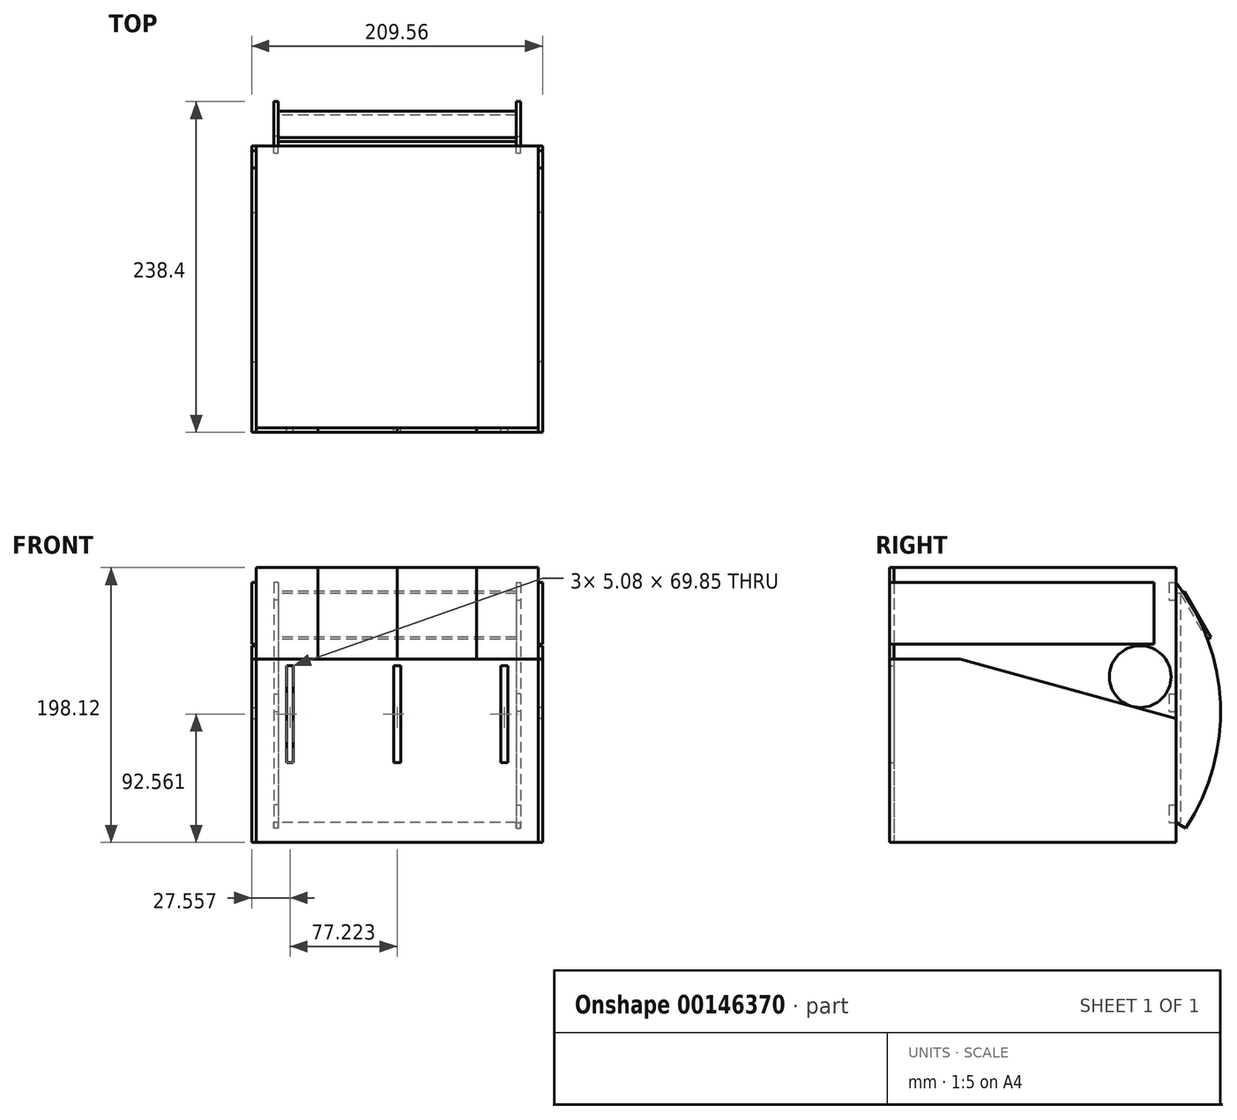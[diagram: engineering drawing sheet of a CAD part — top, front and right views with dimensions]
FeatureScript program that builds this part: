
annotation { "Feature Type Name" : "Feature", "Feature Type Description" : "" }
export const myFeature = defineFeature(function(context is Context, id is Id, definition is map)
    precondition{}
    {
        {
            var Q0;
            Q0=qCreatedBy(makeId("Top.planeOp"),FACE);
            var sketch = newSketch(context, id + "F0", { "sketchPlane" : qUnion([Q0])});
            skLineSegment(sketch, "E0.bottom", {"start": v(101.6, 101.6) * mm, "end": v(-101.6, 101.6) * mm});
            skLineSegment(sketch, "E0.top", {"start": v(101.6, -101.6) * mm, "end": v(-101.6, -101.6) * mm});
            skLineSegment(sketch, "E0.left", {"start": v(101.6, 101.6) * mm, "end": v(101.6, -101.6) * mm});
            skLineSegment(sketch, "E0.right", {"start": v(-101.6, 101.6) * mm, "end": v(-101.6, -101.6) * mm});
            skPoint(sketch, "E0.middle", {"position": v(0, 0) * mm});
            skSolve(sketch);
        }
        {
            var Q0;
            Q0=makeQuery(id+"F0.imprint","IMPRINT",FACE,{"disambiguationData":[TD([[makeQuery(id+"F0.imprint","IMPRINT",EDGE,{"derivedFrom":sQuery(id+"F0.wireOp",EDGE,"E0.bottom")}),1.0]])]});
            extrude(context, id + "F1", {"entities" : qUnion([Q0]), "depth" : 198.12 * mm});
        }
        {
            var Q0;
            Q0=makeQuery(id+"F1.opExtrude","SWEPT_FACE",FACE,{"disambiguationData":[OSD([sQuery(id+"F0.wireOp",EDGE,"E0.top")])]});
            var sketch = newSketch(context, id + "F2", { "sketchPlane" : qUnion([Q0])});
            skLineSegment(sketch, "E1.bottom", {"start": v(-101.6, 132.08) * mm, "end": v(101.6, 132.08) * mm});
            skLineSegment(sketch, "E1.top", {"start": v(-101.6, 0) * mm, "end": v(101.6, 0) * mm});
            skLineSegment(sketch, "E1.left", {"start": v(-101.6, 132.08) * mm, "end": v(-101.6, 0) * mm});
            skLineSegment(sketch, "E1.right", {"start": v(101.6, 132.08) * mm, "end": v(101.6, 0) * mm});
            skLineSegment(sketch, "E2", {"start": v(0, 132.08) * mm, "end": v(0, 0) * mm, "construction": true});
            skLineSegment(sketch, "E3.bottom", {"start": v(2.54, 127.49) * mm, "end": v(-2.54, 127.49) * mm});
            skLineSegment(sketch, "E3.top", {"start": v(2.54, 57.64) * mm, "end": v(-2.54, 57.64) * mm});
            skLineSegment(sketch, "E3.left", {"start": v(2.54, 127.49) * mm, "end": v(2.54, 57.64) * mm});
            skLineSegment(sketch, "E3.right", {"start": v(-2.54, 127.49) * mm, "end": v(-2.54, 57.64) * mm});
            skPoint(sketch, "E3.middle", {"position": v(0, 92.56) * mm});
            skLineSegment(sketch, "E4.bottom", {"start": v(-74.68, 127.49) * mm, "end": v(-79.76, 127.49) * mm});
            skLineSegment(sketch, "E4.top", {"start": v(-74.68, 57.64) * mm, "end": v(-79.76, 57.64) * mm});
            skLineSegment(sketch, "E4.left", {"start": v(-74.68, 127.49) * mm, "end": v(-74.68, 57.64) * mm});
            skLineSegment(sketch, "E4.right", {"start": v(-79.76, 127.49) * mm, "end": v(-79.76, 57.64) * mm});
            skPoint(sketch, "E4.middle", {"position": v(-77.22, 92.56) * mm});
            skLineSegment(sketch, "E5.MirrorCS", {"start": v(74.68, 57.64) * mm, "end": v(79.76, 57.64) * mm});
            skLineSegment(sketch, "E6.MirrorCS", {"start": v(74.68, 127.49) * mm, "end": v(79.76, 127.49) * mm});
            skPoint(sketch, "E7.MirrorP", {"position": v(77.22, 92.56) * mm});
            skLineSegment(sketch, "E8.MirrorCS", {"start": v(79.76, 127.49) * mm, "end": v(79.76, 57.64) * mm});
            skLineSegment(sketch, "E9.MirrorCS", {"start": v(74.68, 127.49) * mm, "end": v(74.68, 57.64) * mm});
            skSolve(sketch);
        }
        {
            var Q0;
            Q0 = qSketchRegion(id + "F2", true);
            extrude(context, id + "F3", {"entities" : qUnion([Q0]), "depth" : 3.17 * mm});
        }
        {
            var Q0;
            Q0=makeQuery(id+"F1.opExtrude","SWEPT_FACE",FACE,{"disambiguationData":[OSD([sQuery(id+"F0.wireOp",EDGE,"E0.top")])]});
            var sketch = newSketch(context, id + "F4", { "sketchPlane" : qUnion([Q0])});
            skLineSegment(sketch, "E10.0", {"start": v(-101.6, 132.08) * mm, "end": v(101.6, 132.08) * mm, "construction": true});
            skLineSegment(sketch, "E11.bottom", {"start": v(-101.6, 132.08) * mm, "end": v(-57.15, 132.08) * mm});
            skLineSegment(sketch, "E11.top", {"start": v(-101.6, 198.12) * mm, "end": v(-57.15, 198.12) * mm});
            skLineSegment(sketch, "E11.left", {"start": v(-101.6, 132.08) * mm, "end": v(-101.6, 198.12) * mm});
            skLineSegment(sketch, "E11.right", {"start": v(-57.15, 132.08) * mm, "end": v(-57.15, 198.12) * mm});
            skLineSegment(sketch, "E12", {"start": v(0, 198.12) * mm, "end": v(0, 0) * mm, "construction": true});
            skLineSegment(sketch, "E13.MirrorCS", {"start": v(101.6, 132.08) * mm, "end": v(57.15, 132.08) * mm});
            skLineSegment(sketch, "E14.MirrorCS", {"start": v(101.6, 132.08) * mm, "end": v(101.6, 198.12) * mm});
            skLineSegment(sketch, "E15.MirrorCS", {"start": v(57.15, 132.08) * mm, "end": v(57.15, 198.12) * mm});
            skLineSegment(sketch, "E16.MirrorCS", {"start": v(101.6, 198.12) * mm, "end": v(57.15, 198.12) * mm});
            skSolve(sketch);
        }
        {
            var Q0;
            Q0 = qSketchRegion(id + "F4", true);
            extrude(context, id + "F5", {"entities" : qUnion([Q0]), "depth" : 3.17 * mm});
        }
        {
            var Q0;
            Q0=makeQuery(id+"F1.opExtrude","SWEPT_FACE",FACE,{"disambiguationData":[OSD([sQuery(id+"F0.wireOp",EDGE,"E0.top")])]});
            var sketch = newSketch(context, id + "F6", { "sketchPlane" : qUnion([Q0])});
            skLineSegment(sketch, "E17.0", {"start": v(-101.6, 132.08) * mm, "end": v(101.6, 132.08) * mm, "construction": true});
            skLineSegment(sketch, "E18.bottom", {"start": v(0, 198.12) * mm, "end": v(57.15, 198.12) * mm});
            skLineSegment(sketch, "E18.top", {"start": v(0, 132.08) * mm, "end": v(57.15, 132.08) * mm});
            skLineSegment(sketch, "E18.left", {"start": v(0, 198.12) * mm, "end": v(0, 132.08) * mm});
            skLineSegment(sketch, "E18.right", {"start": v(57.15, 198.12) * mm, "end": v(57.15, 132.08) * mm});
            skSolve(sketch);
        }
        {
            var Q0;
            Q0 = qSketchRegion(id + "F6", true);
            extrude(context, id + "F7", {"entities" : qUnion([Q0]), "depth" : 3.17 * mm});
        }
        {
            var Q0;
            Q0=makeQuery(id+"F1.opExtrude","SWEPT_FACE",FACE,{"disambiguationData":[OSD([sQuery(id+"F0.wireOp",EDGE,"E0.left")])]});
            var sketch = newSketch(context, id + "F8", { "sketchPlane" : qUnion([Q0])});
            skLineSegment(sketch, "E19.0", {"start": v(-104.78, 198.12) * mm, "end": v(-104.78, 132.08) * mm, "construction": true});
            skLineSegment(sketch, "E20.bottom", {"start": v(-104.78, 187.33) * mm, "end": v(85.72, 187.33) * mm});
            skLineSegment(sketch, "E20.top", {"start": v(-104.78, 142.88) * mm, "end": v(85.72, 142.88) * mm});
            skLineSegment(sketch, "E20.left", {"start": v(-104.78, 187.33) * mm, "end": v(-104.78, 142.88) * mm});
            skLineSegment(sketch, "E20.right", {"start": v(85.73, 187.33) * mm, "end": v(85.73, 142.88) * mm});
            skPoint(sketch, "E21", {"position": v(-104.78, 165.1) * mm});
            skSolve(sketch);
        }
        {
            var Q0;
            Q0 = qSketchRegion(id + "F8", true);
            extrude(context, id + "F9", {"entities" : qUnion([Q0]), "depth" : 3.17 * mm});
        }
        {
            var Q0;
            Q0=makeQuery(id+"F1.opExtrude","SWEPT_FACE",FACE,{"disambiguationData":[OSD([sQuery(id+"F0.wireOp",EDGE,"E0.left")])]});
            var sketch = newSketch(context, id + "F10", { "sketchPlane" : qUnion([Q0])});
            skLineSegment(sketch, "E22.0", {"start": v(-104.78, 132.08) * mm, "end": v(-104.78, 0) * mm, "construction": true});
            skLineSegment(sketch, "E23", {"start": v(101.6, 0) * mm, "end": v(-104.78, 0) * mm});
            skLineSegment(sketch, "E24", {"start": v(-104.78, 132.08) * mm, "end": v(-104.78, 0) * mm});
            skLineSegment(sketch, "E25", {"start": v(-104.78, 132.08) * mm, "end": v(-53.98, 132.08) * mm});
            skLineSegment(sketch, "E26", {"start": v(-53.98, 132.08) * mm, "end": v(101.6, 89.4) * mm});
            skLineSegment(sketch, "E27", {"start": v(101.6, 89.4) * mm, "end": v(101.6, 0) * mm});
            skSolve(sketch);
        }
        {
            var Q0;
            Q0 = qSketchRegion(id + "F10", true);
            extrude(context, id + "F11", {"entities" : qUnion([Q0]), "depth" : 3.17 * mm});
        }
        {
            var Q0;
            Q0=makeQuery(id+"F1.opExtrude","SWEPT_FACE",FACE,{"disambiguationData":[OSD([sQuery(id+"F0.wireOp",EDGE,"E0.left")])]});
            var sketch = newSketch(context, id + "F12", { "sketchPlane" : qUnion([Q0])});
            skCircle(sketch, "E28", {"center": v(75.76, 119.53) * mm, "radius": 22.23 * mm});
            skSolve(sketch);
        }
        {
            var Q0;
            Q0 = qSketchRegion(id + "F12", true);
            extrude(context, id + "F13", {"entities" : qUnion([Q0]), "depth" : 3.17 * mm});
        }
        {
            var Q0;
            Q0=makeQuery(id+"F1.opExtrude","SWEPT_FACE",FACE,{"disambiguationData":[OSD([sQuery(id+"F0.wireOp",EDGE,"E0.right")])]});
            cPlane(context, id + "F14", {"entities" : qUnion([Q0]), "cplaneType" : CPlaneType.OFFSET, "offset" : 101.6 * mm, "oppositeDirection" : true, "width" : 152.4 * mm, "height" : 152.4 * mm});
        }
        {
            var Q0;
            Q0=qCreatedBy(id+"F14.planeOp",FACE);
            var sketch = newSketch(context, id + "F15", { "sketchPlane" : qUnion([Q0])});
            skLineSegment(sketch, "E29.0", {"start": v(-101.6, 198.12) * mm, "end": v(-101.6, 0) * mm, "construction": true});
            skArc(sketch, "E30", {"start": v(-101.6, 187.34) * mm, "mid": v(-133.5, 99.98) * mm, "end": v(-108.7, 10.34) * mm});
            skLineSegment(sketch, "E31", {"start": v(-108.7, 10.34) * mm, "end": v(-101.6, 14.21) * mm});
            skLineSegment(sketch, "E32", {"start": v(-101.6, 187.34) * mm, "end": v(-101.6, 14.21) * mm});
            skSolve(sketch);
        }
        {
            var Q0;
            Q0=makeQuery(id+"F15.imprint","IMPRINT",FACE,{"disambiguationData":[TD([[makeQuery(id+"F15.imprint","IMPRINT",EDGE,{"derivedFrom":sQuery(id+"F15.wireOp",EDGE,"E30")}),1.0]])]});
            extrude(context, id + "F16", {"entities" : qUnion([Q0]), "depth" : 3.17 * mm});
        }
        {
            var Q0;
            Q0=makeQuery(id+"F16.opExtrude","SWEPT_BODY",BODY,{"disambiguationData":[OSD([sQuery(id+"F15.wireOp",EDGE,"E30"),sQuery(id+"F15.wireOp",EDGE,"E31"),sQuery(id+"F15.wireOp",EDGE,"E32")])]});
            var Q1;
            Q1=makeQuery(id+"F1.opExtrude","CAP_EDGE",EDGE,{"disambiguationData":[OSD([sQuery(id+"F0.wireOp",EDGE,"E0.bottom")])],"isStart":false});
            var Q2;
            Q2=makeQuery(id+"F1.opExtrude","CAP_EDGE",EDGE,{"disambiguationData":[OSD([sQuery(id+"F0.wireOp",EDGE,"E0.bottom")])],"isStart":false});
            transform(context, id + "F17", {"entities" : qUnion([Q0]), "transformType" : TransformType.TRANSLATION_DISTANCE, "transformDirection" : qUnion([Q2]), "distance" : 88.9 * mm, "oppositeDirection" : true, "makeCopy" : false});
        }
        {
            var Q0;
            Q0=makeQuery(id+"F16.opExtrude","SWEPT_FACE",FACE,{"disambiguationData":[OSD([sQuery(id+"F15.wireOp",EDGE,"E32")])]});
            var sketch = newSketch(context, id + "F18", { "sketchPlane" : qUnion([Q0])});
            skLineSegment(sketch, "E33.bottom", {"start": v(85.72, 187.34) * mm, "end": v(88.9, 187.34) * mm});
            skLineSegment(sketch, "E33.top", {"start": v(85.72, 174.64) * mm, "end": v(88.9, 174.64) * mm});
            skLineSegment(sketch, "E33.left", {"start": v(85.72, 187.34) * mm, "end": v(85.72, 174.64) * mm});
            skLineSegment(sketch, "E33.right", {"start": v(88.9, 187.34) * mm, "end": v(88.9, 174.64) * mm});
            skLineSegment(sketch, "E34.bottom", {"start": v(85.72, 14.21) * mm, "end": v(88.9, 14.21) * mm});
            skLineSegment(sketch, "E34.top", {"start": v(85.73, 26.91) * mm, "end": v(88.9, 26.91) * mm});
            skLineSegment(sketch, "E34.left", {"start": v(85.72, 14.21) * mm, "end": v(85.72, 26.91) * mm});
            skLineSegment(sketch, "E34.right", {"start": v(88.9, 14.21) * mm, "end": v(88.9, 26.91) * mm});
            skLineSegment(sketch, "E35", {"start": v(87.31, 187.34) * mm, "end": v(87.31, 14.21) * mm, "construction": true});
            skPoint(sketch, "E36", {"position": v(87.31, 100.77) * mm});
            skLineSegment(sketch, "E37.bottom", {"start": v(88.9, 107.12) * mm, "end": v(85.72, 107.12) * mm});
            skLineSegment(sketch, "E37.top", {"start": v(88.9, 94.42) * mm, "end": v(85.72, 94.42) * mm});
            skLineSegment(sketch, "E37.left", {"start": v(88.9, 107.12) * mm, "end": v(88.9, 94.42) * mm});
            skLineSegment(sketch, "E37.right", {"start": v(85.72, 107.12) * mm, "end": v(85.72, 94.42) * mm});
            skSolve(sketch);
        }
        {
            var Q0;
            Q0 = qSketchRegion(id + "F18", true);
            extrude(context, id + "F19", {"entities" : qUnion([Q0]), "depth" : 5.08 * mm});
        }
        {
            var Q0;
            Q0=makeQuery(id+"F16.opExtrude","SWEPT_BODY",BODY,{"disambiguationData":[OSD([sQuery(id+"F15.wireOp",EDGE,"E30"),sQuery(id+"F15.wireOp",EDGE,"E31"),sQuery(id+"F15.wireOp",EDGE,"E32")])]});
            var Q1;
            Q1=makeQuery(id+"F11.opExtrude","SWEPT_BODY",BODY,{"disambiguationData":[OSD([sQuery(id+"F10.wireOp",EDGE,"E23"),sQuery(id+"F10.wireOp",EDGE,"E24"),sQuery(id+"F10.wireOp",EDGE,"E25"),sQuery(id+"F10.wireOp",EDGE,"E26"),sQuery(id+"F10.wireOp",EDGE,"E27")])]});
            var Q2;
            Q2=makeQuery(id+"F9.opExtrude","SWEPT_BODY",BODY,{"disambiguationData":[OSD([sQuery(id+"F8.wireOp",EDGE,"E20.bottom"),sQuery(id+"F8.wireOp",EDGE,"E20.top"),sQuery(id+"F8.wireOp",EDGE,"E20.left"),sQuery(id+"F8.wireOp",EDGE,"E20.right")])]});
            var Q3;
            Q3=makeQuery(id+"F13.opExtrude","SWEPT_BODY",BODY,{"disambiguationData":[OSD([sQuery(id+"F12.wireOp",EDGE,"E28")])]});
            var Q4;
            Q4=makeQuery(id+"F19.opExtrude","SWEPT_BODY",BODY,{"disambiguationData":[OSD([sQuery(id+"F18.wireOp",EDGE,"E37.bottom"),sQuery(id+"F18.wireOp",EDGE,"E37.top"),sQuery(id+"F18.wireOp",EDGE,"E37.left"),sQuery(id+"F18.wireOp",EDGE,"E37.right")])]});
            var Q5;
            Q5=makeQuery(id+"F19.opExtrude","SWEPT_BODY",BODY,{"disambiguationData":[OSD([sQuery(id+"F18.wireOp",EDGE,"E34.bottom"),sQuery(id+"F18.wireOp",EDGE,"E34.top"),sQuery(id+"F18.wireOp",EDGE,"E34.left"),sQuery(id+"F18.wireOp",EDGE,"E34.right")])]});
            var Q6;
            Q6=makeQuery(id+"F19.opExtrude","SWEPT_BODY",BODY,{"disambiguationData":[OSD([sQuery(id+"F18.wireOp",EDGE,"E33.bottom"),sQuery(id+"F18.wireOp",EDGE,"E33.top"),sQuery(id+"F18.wireOp",EDGE,"E33.left"),sQuery(id+"F18.wireOp",EDGE,"E33.right")])]});
            var Q7;
            Q7=qCreatedBy(id+"F14.planeOp",FACE);
            mirror(context, id + "F20", {"entities" : qUnion([Q0, Q1, Q2, Q3, Q4, Q5, Q6]), "mirrorPlane" : qUnion([Q7])});
        }
        {
            var Q0;
            Q0=makeQuery(id+"F19.opExtrude","SWEPT_BODY",BODY,{"disambiguationData":[OSD([sQuery(id+"F18.wireOp",EDGE,"E33.bottom"),sQuery(id+"F18.wireOp",EDGE,"E33.top"),sQuery(id+"F18.wireOp",EDGE,"E33.left"),sQuery(id+"F18.wireOp",EDGE,"E33.right")])]});
            var Q1;
            Q1=makeQuery(id+"F19.opExtrude","SWEPT_BODY",BODY,{"disambiguationData":[OSD([sQuery(id+"F18.wireOp",EDGE,"E37.bottom"),sQuery(id+"F18.wireOp",EDGE,"E37.top"),sQuery(id+"F18.wireOp",EDGE,"E37.left"),sQuery(id+"F18.wireOp",EDGE,"E37.right")])]});
            var Q2;
            Q2=makeQuery(id+"F19.opExtrude","SWEPT_BODY",BODY,{"disambiguationData":[OSD([sQuery(id+"F18.wireOp",EDGE,"E34.bottom"),sQuery(id+"F18.wireOp",EDGE,"E34.top"),sQuery(id+"F18.wireOp",EDGE,"E34.left"),sQuery(id+"F18.wireOp",EDGE,"E34.right")])]});
            var Q3;
            Q3=makeQuery(id+"F20.opPattern","COPY",BODY,{"derivedFrom":makeQuery(id+"F19.opExtrude","SWEPT_BODY",BODY,{"disambiguationData":[OSD([sQuery(id+"F18.wireOp",EDGE,"E34.bottom"),sQuery(id+"F18.wireOp",EDGE,"E34.top"),sQuery(id+"F18.wireOp",EDGE,"E34.left"),sQuery(id+"F18.wireOp",EDGE,"E34.right")])]}),"instanceName":"1"});
            var Q4;
            Q4=makeQuery(id+"F20.opPattern","COPY",BODY,{"derivedFrom":makeQuery(id+"F19.opExtrude","SWEPT_BODY",BODY,{"disambiguationData":[OSD([sQuery(id+"F18.wireOp",EDGE,"E37.bottom"),sQuery(id+"F18.wireOp",EDGE,"E37.top"),sQuery(id+"F18.wireOp",EDGE,"E37.left"),sQuery(id+"F18.wireOp",EDGE,"E37.right")])]}),"instanceName":"1"});
            var Q5;
            Q5=makeQuery(id+"F20.opPattern","COPY",BODY,{"derivedFrom":makeQuery(id+"F19.opExtrude","SWEPT_BODY",BODY,{"disambiguationData":[OSD([sQuery(id+"F18.wireOp",EDGE,"E33.bottom"),sQuery(id+"F18.wireOp",EDGE,"E33.top"),sQuery(id+"F18.wireOp",EDGE,"E33.left"),sQuery(id+"F18.wireOp",EDGE,"E33.right")])]}),"instanceName":"1"});
            var Q6;
            Q6=makeQuery(id+"F1.opExtrude","SWEPT_BODY",BODY,{"disambiguationData":[OSD([sQuery(id+"F0.wireOp",EDGE,"E0.bottom"),sQuery(id+"F0.wireOp",EDGE,"E0.top"),sQuery(id+"F0.wireOp",EDGE,"E0.left"),sQuery(id+"F0.wireOp",EDGE,"E0.right")])]});
            booleanBodies(context, id + "F21", {"operationType" : BooleanOperationType.SUBTRACTION, "tools" : qUnion([Q0, Q1, Q2, Q3, Q4, Q5]), "targets" : qUnion([Q6]), "keepTools" : true});
        }
        {
            var Q0;
            Q0=makeQuery(id+"F1.opExtrude","SWEPT_FACE",FACE,{"disambiguationData":[OSD([sQuery(id+"F0.wireOp",EDGE,"E0.bottom")])]});
            var sketch = newSketch(context, id + "F22", { "sketchPlane" : qUnion([Q0])});
            skLineSegment(sketch, "E38.bottom", {"start": v(-85.72, 14.21) * mm, "end": v(85.72, 14.21) * mm});
            skLineSegment(sketch, "E38.top", {"start": v(-85.73, 179.31) * mm, "end": v(85.72, 179.31) * mm});
            skLineSegment(sketch, "E38.left", {"start": v(-85.72, 14.21) * mm, "end": v(-85.72, 179.31) * mm});
            skLineSegment(sketch, "E38.right", {"start": v(85.72, 14.21) * mm, "end": v(85.72, 179.31) * mm});
            skSolve(sketch);
        }
        {
            var Q0;
            Q0 = qSketchRegion(id + "F22", true);
            extrude(context, id + "F23", {"entities" : qUnion([Q0]), "depth" : 3.17 * mm});
        }
        {
            var Q0;
            Q0=makeQuery(id+"F23.opExtrude","CAP_FACE",FACE,{"disambiguationData":[OSD([sQuery(id+"F22.wireOp",EDGE,"E38.bottom"),sQuery(id+"F22.wireOp",EDGE,"E38.top"),sQuery(id+"F22.wireOp",EDGE,"E38.left"),sQuery(id+"F22.wireOp",EDGE,"E38.right")])],"isStart":false});
            var sketch = newSketch(context, id + "F24", { "sketchPlane" : qUnion([Q0])});
            skLineSegment(sketch, "E39.bottom", {"start": v(-85.72, 179.31) * mm, "end": v(85.72, 179.31) * mm});
            skLineSegment(sketch, "E39.top", {"start": v(-85.72, 141.21) * mm, "end": v(85.72, 141.21) * mm});
            skLineSegment(sketch, "E39.left", {"start": v(-85.72, 179.31) * mm, "end": v(-85.72, 141.21) * mm});
            skLineSegment(sketch, "E39.right", {"start": v(85.72, 179.31) * mm, "end": v(85.72, 141.21) * mm});
            skSolve(sketch);
        }
        {
            var Q0;
            Q0=makeQuery(id+"F24.imprint","IMPRINT",FACE,{"disambiguationData":[TD([[makeQuery(id+"F24.imprint","IMPRINT",EDGE,{"derivedFrom":sQuery(id+"F24.wireOp",EDGE,"E39.bottom")}),-1.0]])]});
            extrude(context, id + "F25", {"entities" : qUnion([Q0]), "depth" : 3.17 * mm});
        }
        {
            var Q0;
            Q0=makeQuery(id+"F25.opExtrude","SWEPT_BODY",BODY,{"disambiguationData":[OSD([sQuery(id+"F24.wireOp",EDGE,"E39.bottom"),sQuery(id+"F24.wireOp",EDGE,"E39.top"),sQuery(id+"F24.wireOp",EDGE,"E39.left"),sQuery(id+"F24.wireOp",EDGE,"E39.right")])]});
            var Q1;
            Q1=makeQuery(id+"F23.opExtrude","CAP_EDGE",EDGE,{"disambiguationData":[OSD([sQuery(id+"F22.wireOp",EDGE,"E38.top")])],"isStart":false});
            transform(context, id + "F26", {"entities" : qUnion([Q0]), "transformType" : TransformType.ROTATION, "transformAxis" : qUnion([Q1]), "angle" : 30 * degree, "oppositeDirection" : true, "makeCopy" : false});
        }
    });
